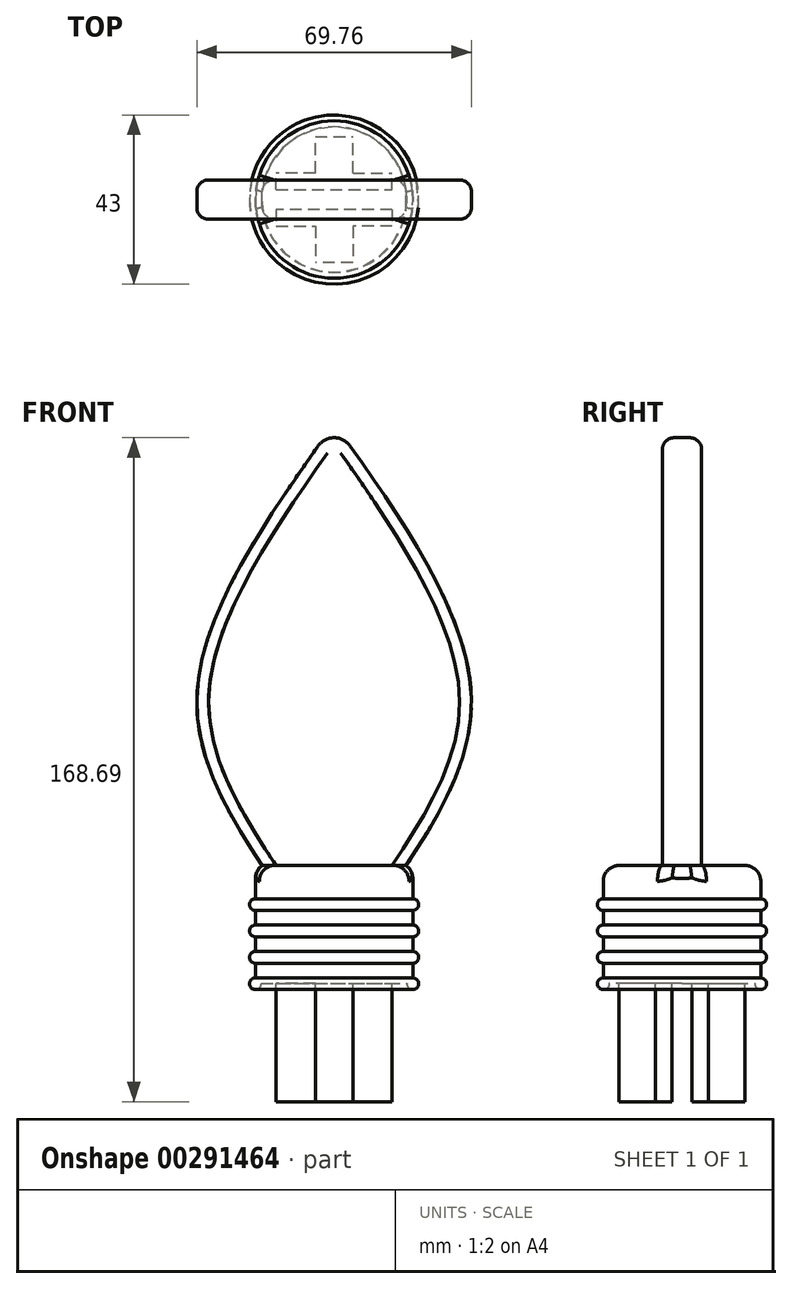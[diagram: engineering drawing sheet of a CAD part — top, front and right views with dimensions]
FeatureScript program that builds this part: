
annotation { "Feature Type Name" : "Feature", "Feature Type Description" : "" }
export const myFeature = defineFeature(function(context is Context, id is Id, definition is map)
    precondition{}
    {
        {
            var Q0;
            Q0=qCreatedBy(makeId("Front.planeOp"),FACE);
            var sketch = newSketch(context, id + "F0", { "sketchPlane" : qUnion([Q0])});
            skFitSpline(sketch, "E0", {"points": [v(-15, -37.06) * mm, v(-34.85, 11.03) * mm, v(0, 80.3) * mm], "startDerivative": vector(-68.3, 102.47) * mm, "endDerivative": vector(92.95, 131.28) * mm});
            skFitSpline(sketch, "E1.MirrorCS", {"points": [v(15, -37.06) * mm, v(34.85, 11.03) * mm, v(0, 80.3) * mm], "startDerivative": vector(68.3, 102.47) * mm, "endDerivative": vector(-92.95, 131.28) * mm});
            skLineSegment(sketch, "E2", {"start": v(-15, -37.06) * mm, "end": v(15, -37.06) * mm});
            skSolve(sketch);
        }
        {
            var Q0;
            Q0=makeQuery(id+"F0.imprint","IMPRINT",FACE,{"disambiguationData":[TD([[makeQuery(id+"F0.imprint","IMPRINT",EDGE,{"derivedFrom":sQuery(id+"F0.wireOp",EDGE,"E0")}),-1.0]])]});
            extrude(context, id + "F1", {"entities" : qUnion([Q0]), "endBound" : BoundingType.SYMMETRIC, "depth" : 10 * mm});
        }
        {
            var Q0;
            Q0=makeQuery(id+"F1.opExtrude","CAP_EDGE",EDGE,{"disambiguationData":[OSD([sQuery(id+"F0.wireOp",EDGE,"E1.MirrorCS")])],"isStart":false});
            var Q1;
            Q1=makeQuery(id+"F1.opExtrude","CAP_EDGE",EDGE,{"disambiguationData":[OSD([sQuery(id+"F0.wireOp",EDGE,"E0")])],"isStart":false});
            var Q2;
            Q2=makeQuery(id+"F1.opExtrude","CAP_EDGE",EDGE,{"disambiguationData":[OSD([sQuery(id+"F0.wireOp",EDGE,"E0")])],"isStart":true});
            var Q3;
            Q3=makeQuery(id+"F1.opExtrude","CAP_EDGE",EDGE,{"disambiguationData":[OSD([sQuery(id+"F0.wireOp",EDGE,"E1.MirrorCS")])],"isStart":true});
            fillet(context, id + "F2", {"entities" : qUnion([Q0, Q1, Q2, Q3]), "radius" : 3 * mm, "tangentPropagation" : true, "allowEdgeOverflow" : false});
        }
        {
            var Q0;
            Q0=makeQuery(id+"F2.opFillet","BLEND_EDGE",EDGE,{"blendedFrom":[makeQuery(id+"F1.opExtrude","CAP_EDGE",EDGE,{"disambiguationData":[OSD([sQuery(id+"F0.wireOp",EDGE,"E0")])],"isStart":true}),makeQuery(id+"F1.opExtrude","CAP_EDGE",EDGE,{"disambiguationData":[OSD([sQuery(id+"F0.wireOp",EDGE,"E1.MirrorCS")])],"isStart":true})],"blendedInto":[]});
            var Q1;
            Q1=makeQuery(id+"F2.opFillet","BLEND_EDGE",EDGE,{"blendedFrom":[makeQuery(id+"F1.opExtrude","CAP_EDGE",EDGE,{"disambiguationData":[OSD([sQuery(id+"F0.wireOp",EDGE,"E0")])],"isStart":false}),makeQuery(id+"F1.opExtrude","CAP_EDGE",EDGE,{"disambiguationData":[OSD([sQuery(id+"F0.wireOp",EDGE,"E1.MirrorCS")])],"isStart":false})],"blendedInto":[]});
            fillet(context, id + "F3", {"entities" : qUnion([Q0, Q1]), "radius" : 5 * mm, "tangentPropagation" : true, "allowEdgeOverflow" : false});
        }
        {
            var Q0;
            Q0=makeQuery(id+"F1.opExtrude","SWEPT_FACE",FACE,{"disambiguationData":[OSD([sQuery(id+"F0.wireOp",EDGE,"E2")])]});
            var sketch = newSketch(context, id + "F4", { "sketchPlane" : qUnion([Q0])});
            skLineSegment(sketch, "E3.0.0", {"start": v(-15, 2) * mm, "end": v(-15, -2) * mm});
            skFitSpline(sketch, "E3.0.1", {"points": [v(-15, 3) * mm, v(-15, 2.78) * mm, v(-14.96, 2.46) * mm, v(-14.82, 2.05) * mm, v(-14.68, 1.75) * mm, v(-14.5, 1.48) * mm, v(-14.24, 1.13) * mm, v(-13.92, 0.84) * mm, v(-13.56, 0.6) * mm, v(-13.27, 0.44) * mm, v(-12.98, 0.3) * mm, v(-12.57, 0.15) * mm, v(-12.04, 0.03) * mm, v(-11.61, 0) * mm, v(-11.4, 0) * mm]});
            skLineSegment(sketch, "E3.0.2", {"start": v(-11.4, -5) * mm, "end": v(11.4, -5) * mm});
            skFitSpline(sketch, "E3.0.3", {"points": [v(11.4, 0) * mm, v(11.61, 0) * mm, v(12.04, 0.03) * mm, v(12.67, 0.18) * mm, v(13.28, 0.42) * mm, v(13.83, 0.76) * mm, v(14.32, 1.2) * mm, v(14.63, 1.65) * mm, v(14.82, 2.04) * mm, v(14.92, 2.35) * mm, v(14.99, 2.67) * mm, v(15, 2.9) * mm, v(15, 3) * mm]});
            skLineSegment(sketch, "E3.0.4", {"start": v(15, -2) * mm, "end": v(15, 2) * mm});
            skFitSpline(sketch, "E3.0.5", {"points": [v(15, 7) * mm, v(15, 7.22) * mm, v(14.96, 7.54) * mm, v(14.82, 7.95) * mm, v(14.68, 8.25) * mm, v(14.5, 8.52) * mm, v(14.24, 8.87) * mm, v(13.92, 9.16) * mm, v(13.56, 9.4) * mm, v(13.27, 9.56) * mm, v(12.98, 9.7) * mm, v(12.57, 9.85) * mm, v(12.04, 9.97) * mm, v(11.61, 10) * mm, v(11.4, 10) * mm]});
            skLineSegment(sketch, "E3.0.6", {"start": v(11.4, 5) * mm, "end": v(-11.4, 5) * mm});
            skFitSpline(sketch, "E3.0.7", {"points": [v(-11.4, 10) * mm, v(-11.61, 10) * mm, v(-12.04, 9.97) * mm, v(-12.67, 9.82) * mm, v(-13.28, 9.58) * mm, v(-13.83, 9.24) * mm, v(-14.32, 8.8) * mm, v(-14.63, 8.35) * mm, v(-14.82, 7.96) * mm, v(-14.92, 7.65) * mm, v(-14.99, 7.33) * mm, v(-15, 7.1) * mm, v(-15, 7) * mm]});
            skLineSegment(sketch, "E4", {"start": v(-15, 0) * mm, "end": v(15, 0) * mm, "construction": true});
            skLineSegment(sketch, "E5", {"start": v(0, 5) * mm, "end": v(0, -5) * mm, "construction": true});
            skCircle(sketch, "E6", {"center": v(0, 0) * mm, "radius": 20 * mm});
            skLineSegment(sketch, "E7", {"start": v(0, 5) * mm, "end": v(0, 20) * mm});
            skSolve(sketch);
        }
        {
            var Q0;
            Q0 = qSketchRegion(id + "F4", true);
            var Q1;
            Q1=makeQuery(id+"F4.imprint","IMPRINT",FACE,{"disambiguationData":[TD([[makeQuery(id+"F4.imprint","IMPRINT",EDGE,{"derivedFrom":sQuery(id+"F4.wireOp",EDGE,"E3.0.0")}),1.0]])]});
            extrude(context, id + "F5", {"entities" : qUnion([Q0, Q1]), "operationType" : NewBodyOperationType.ADD, "endBound" : BoundingType.SYMMETRIC, "depth" : 10 * mm});
        }
        {
            var Q0;
            Q0=makeQuery(id+"F5.opExtrude","CAP_EDGE",EDGE,{"disambiguationData":[OSD([sQuery(id+"F4.wireOp",EDGE,"E6")])],"isStart":true});
            fillet(context, id + "F6", {"entities" : qUnion([Q0]), "radius" : 4 * mm, "tangentPropagation" : true, "allowEdgeOverflow" : false});
        }
        {
            var Q0;
            Q0=makeQuery(id+"F5.opExtrude","CAP_FACE",FACE,{"disambiguationData":[OSD([sQuery(id+"F4.wireOp",EDGE,"E6")])],"isStart":false});
            extrude(context, id + "F7", {"entities" : qUnion([Q0]), "operationType" : NewBodyOperationType.ADD, "depth" : 20 * mm});
        }
        {
            var Q0;
            Q0=qCreatedBy(makeId("Front.planeOp"),FACE);
            var sketch = newSketch(context, id + "F8", { "sketchPlane" : qUnion([Q0])});
            skLineSegment(sketch, "E8", {"start": v(20, -35.32) * mm, "end": v(20, -62.06) * mm});
            skLineSegment(sketch, "E9", {"start": v(-20, -62.06) * mm, "end": v(-20, -35.32) * mm});
            skLineSegment(sketch, "E10", {"start": v(-20, -48.69) * mm, "end": v(20, -48.69) * mm, "construction": true});
            skCircle(sketch, "E11", {"center": v(20, -48.69) * mm, "radius": 1.5 * mm});
            skCircle(sketch, "E12.1.0.0", {"center": v(20, -55.39) * mm, "radius": 1.5 * mm});
            skCircle(sketch, "E12.2.0.0", {"center": v(20, -62.09) * mm, "radius": 1.5 * mm});
            skLineSegment(sketch, "E12.direction1", {"start": v(20, -48.69) * mm, "end": v(20, -55.39) * mm, "construction": true});
            skCircle(sketch, "E13.MirrorC", {"center": v(20, -41.99) * mm, "radius": 1.5 * mm});
            skCircle(sketch, "E14.MirrorC", {"center": v(20, -35.29) * mm, "radius": 1.5 * mm});
            skLineSegment(sketch, "E15", {"start": v(0, -35.91) * mm, "end": v(0, -62.18) * mm, "construction": true});
            skSolve(sketch);
        }
        {
            var Q0;
            Q0=makeQuery(id+"F8.imprint","IMPRINT",FACE,{"disambiguationData":[TD([[makeQuery(id+"F8.imprint","IMPRINT",EDGE,{"derivedFrom":sQuery(id+"F8.wireOp",EDGE,"E14.MirrorC")}),-1.0]])]});
            var Q1;
            {var subQ0=sQuery(id+"F8.wireOp",EDGE,"E13.MirrorC");var subQ1=sQuery(id+"F8.wireOp",EDGE,"E8");var subQ2=makeQuery(id+"F8.imprint","INTERSECT",VERTEX,{"disambiguationData":[OD(0.0)],"derivedFrom":[subQ1,subQ0]});Q1=makeQuery(id+"F8.imprint","IMPRINT",FACE,{"disambiguationData":[TD([[makeQuery(id+"F8.imprint","IMPRINT",EDGE,{"disambiguationData":[TD([[subQ2,1.0]])],"derivedFrom":subQ1}),1.0]])]});}
            var Q2;
            {var subQ0=sQuery(id+"F8.wireOp",EDGE,"E11");var subQ1=sQuery(id+"F8.wireOp",EDGE,"E8");var subQ2=makeQuery(id+"F8.imprint","INTERSECT",VERTEX,{"disambiguationData":[OD(0.0)],"derivedFrom":[subQ1,subQ0]});Q2=makeQuery(id+"F8.imprint","IMPRINT",FACE,{"disambiguationData":[TD([[makeQuery(id+"F8.imprint","IMPRINT",EDGE,{"disambiguationData":[TD([[subQ2,1.0]])],"derivedFrom":subQ1}),1.0]])]});}
            var Q3;
            {var subQ0=sQuery(id+"F8.wireOp",EDGE,"E12.1.0.0");var subQ1=sQuery(id+"F8.wireOp",EDGE,"E8");var subQ2=makeQuery(id+"F8.imprint","INTERSECT",VERTEX,{"disambiguationData":[OD(0.0)],"derivedFrom":[subQ1,subQ0]});Q3=makeQuery(id+"F8.imprint","IMPRINT",FACE,{"disambiguationData":[TD([[makeQuery(id+"F8.imprint","IMPRINT",EDGE,{"disambiguationData":[TD([[subQ2,1.0]])],"derivedFrom":subQ1}),1.0]])]});}
            var Q4;
            Q4=makeQuery(id+"F8.imprint","IMPRINT",FACE,{"disambiguationData":[TD([[makeQuery(id+"F8.imprint","IMPRINT",EDGE,{"derivedFrom":sQuery(id+"F8.wireOp",EDGE,"E12.2.0.0")}),1.0]])]});
            var Q5;
            {var subQ0=sQuery(id+"F4.wireOp",EDGE,"E6");Q5=makeQuery(id+"F7.boolean.opBoolean","MERGE",FACE,{"derivedFrom":[makeQuery(id+"F5.opExtrude","SWEPT_FACE",FACE,{"disambiguationData":[OSD([subQ0])]}),makeQuery(id+"F7.opExtrude","SWEPT_FACE",FACE,{"disambiguationData":[OSD([subQ0])]})]});}
            revolve(context, id + "F9", {"operationType" : NewBodyOperationType.ADD, "entities" : qUnion([Q0, Q1, Q2, Q3, Q4]), "axis" : qUnion([Q5]), "revolveType" : RevolveType.FULL});
        }
        {
            var Q0;
            Q0=makeQuery(id+"F7.opExtrude","CAP_FACE",FACE,{"disambiguationData":[OSD([sQuery(id+"F4.wireOp",EDGE,"E6")])],"isStart":false});
            var sketch = newSketch(context, id + "F10", { "sketchPlane" : qUnion([Q0])});
            skCircle(sketch, "E16.0.0", {"center": v(0, 0) * mm, "radius": 18.5 * mm});
            skLineSegment(sketch, "E17.0", {"start": v(-4.75, 16) * mm, "end": v(-0.25, 16) * mm});
            skLineSegment(sketch, "E17.1", {"start": v(-0.25, 2.5) * mm, "end": v(-14.75, 2.5) * mm});
            skLineSegment(sketch, "E17.2", {"start": v(-14.75, 2.5) * mm, "end": v(-14.75, 6.75) * mm});
            skLineSegment(sketch, "E17.3", {"start": v(-14.75, 6.75) * mm, "end": v(-4.75, 6.75) * mm});
            skLineSegment(sketch, "E17.4", {"start": v(-4.75, 6.75) * mm, "end": v(-4.75, 16) * mm});
            skLineSegment(sketch, "E18.MirrorCS", {"start": v(4.75, 16) * mm, "end": v(0.25, 16) * mm});
            skLineSegment(sketch, "E19.MirrorCS", {"start": v(4.75, 6.75) * mm, "end": v(4.75, 16) * mm});
            skLineSegment(sketch, "E20.MirrorCS", {"start": v(14.75, 6.75) * mm, "end": v(4.75, 6.75) * mm});
            skLineSegment(sketch, "E21.MirrorCS", {"start": v(14.75, 2.5) * mm, "end": v(14.75, 6.75) * mm});
            skLineSegment(sketch, "E22.MirrorCS", {"start": v(0.25, 2.5) * mm, "end": v(14.75, 2.5) * mm});
            skLineSegment(sketch, "E23.MirrorCS", {"start": v(4.75, -6.75) * mm, "end": v(4.75, -16) * mm});
            skLineSegment(sketch, "E24.MirrorCS", {"start": v(14.75, -2.5) * mm, "end": v(14.75, -6.75) * mm});
            skLineSegment(sketch, "E25.MirrorCS", {"start": v(4.75, -6.75) * mm, "end": v(14.75, -6.75) * mm});
            skLineSegment(sketch, "E26.MirrorCS", {"start": v(4.75, -16) * mm, "end": v(0.25, -16) * mm});
            skLineSegment(sketch, "E27.MirrorCS", {"start": v(-4.75, -16) * mm, "end": v(-0.25, -16) * mm});
            skLineSegment(sketch, "E28.MirrorCS", {"start": v(-4.75, -6.75) * mm, "end": v(-4.75, -16) * mm});
            skLineSegment(sketch, "E29.MirrorCS", {"start": v(-14.75, -2.5) * mm, "end": v(-14.75, -6.75) * mm});
            skLineSegment(sketch, "E30.MirrorCS", {"start": v(-4.75, -6.75) * mm, "end": v(-14.75, -6.75) * mm});
            skLineSegment(sketch, "E31", {"start": v(-14.75, -2.5) * mm, "end": v(-14.75, 2.5) * mm});
            skLineSegment(sketch, "E32", {"start": v(14.75, -2.5) * mm, "end": v(14.75, 2.5) * mm});
            skLineSegment(sketch, "E33", {"start": v(0.25, 16) * mm, "end": v(-0.25, 16) * mm});
            skLineSegment(sketch, "E34", {"start": v(-0.25, 2.5) * mm, "end": v(0.25, 2.5) * mm});
            skLineSegment(sketch, "E35", {"start": v(-0.25, -16) * mm, "end": v(0.25, -16) * mm});
            skLineSegment(sketch, "E36", {"start": v(0, 16) * mm, "end": v(0, -16) * mm});
            skLineSegment(sketch, "E37", {"start": v(-14.75, -2.5) * mm, "end": v(14.75, -2.5) * mm});
            skSolve(sketch);
        }
        {
            var Q0;
            {var subQ1=sQuery(id+"F10.wireOp",EDGE,"E17.0");Q0=makeQuery(id+"F10.imprint","IMPRINT",FACE,{"disambiguationData":[TD([[makeQuery(id+"F10.imprint","IMPRINT",EDGE,{"derivedFrom":subQ1}),-1.0]])]});}
            var Q1;
            {var subQ0=sQuery(id+"F10.wireOp",EDGE,"E18.MirrorCS");Q1=makeQuery(id+"F10.imprint","IMPRINT",FACE,{"disambiguationData":[TD([[makeQuery(id+"F10.imprint","IMPRINT",EDGE,{"derivedFrom":subQ0}),1.0]])]});}
            var Q2;
            {var subQ6=sQuery(id+"F10.wireOp",EDGE,"E27.MirrorCS");Q2=makeQuery(id+"F10.imprint","IMPRINT",FACE,{"disambiguationData":[TD([[makeQuery(id+"F10.imprint","IMPRINT",EDGE,{"derivedFrom":subQ6}),1.0]])]});}
            var Q3;
            Q3=makeQuery(id+"F10.imprint","IMPRINT",FACE,{"disambiguationData":[TD([[makeQuery(id+"F10.imprint","IMPRINT",EDGE,{"derivedFrom":sQuery(id+"F10.wireOp",EDGE,"E23.MirrorCS")}),-1.0]])]});
            extrude(context, id + "F11", {"entities" : qUnion([Q0, Q1, Q2, Q3]), "operationType" : NewBodyOperationType.ADD, "depth" : 30 * mm});
        }
    });
